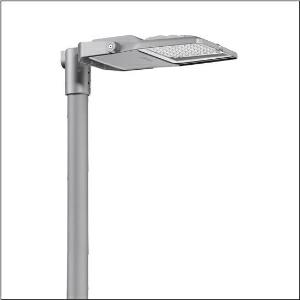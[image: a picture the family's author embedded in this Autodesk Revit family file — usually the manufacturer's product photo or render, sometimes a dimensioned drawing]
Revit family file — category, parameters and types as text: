
# Revit family: floodlight_fl_21_iq_mini___pl43_5xa7772c2a3a_c494
name_source: partatom
category: Lighting Fixtures
units: mm (PartAtom-declared; Revit-internal decimal feet)

## family parameters
Cut with Voids When Loaded = No
Host = Face
Light Source = No
Part Type = Normal
Room Calculation Point = No
Round Connector Dimension = Use Diameter
Shared = No

## types (1)
- --- (1 x LED, 12520 lm, 87.2 W, 3000K)
    Apparent Load = 87 VA
    CIE Flux Codes = 27 78 99 100 100
    Color Rendering = 70
    Color Temperature = 3000K
    Default Elevation = 1800 mm
    Description = Floodlight FL 21 iQ mini, floodlight, primary light control with lens, of PMMA, primary optical cover: protective disc, of toughened safety glass, transparent, light distribution: PL43, light emission: direct distribution, installation type: surface-mounted, LED, High Power LED, rated luminous flux: 12.520lm, luminous efficacy: 144lm/W, light colour: 730, colour temperature: 3000K, control: Auto-Match, Temp-Guard, Night-Set, Smart-Wire, Desk-Remote (wireless, voltage-free reading and setting of iQ features in the workshop via application-optimized NFC function/RFID function), optimised constant luminous flux control (CLO 2.0), Light-Fading, Lumen-Switch, with terminal, 6-pole, mains connection: 220..240V, AC, 50/60Hz, start of lifetime: 87W, end of service life: 92W, reduction: 40W, luminaire housing, of diecast aluminium, powder-coated, Siteco® metallic grey (DB 702S), corrosivity category C5 mid according to DIN EN ISO 12944, sealing non-destructively replaceable, please order mast flange separately, mast bracket, of steel, galvanised, powder-coated, protection rating (complete): IP66, insulation class (complete): insulation class II (safety insulation), certification: CE, ENEC, VDE, protection symbol: D, impact resistance: IK08, permissible operating ambient temperature: -40..+40°C, permissible operating ambient temperature for outdoor applications: -40..+50°C, standard: DIN EN 12944, LABS conformity tested according to VDMA 24364:2018-05, packaging unit: 1 piece

Light Distribution: PL43
    Height = 70 mm
    Lamp = 1 x LED
    Lamp Light Flux = 12520 lm
    Lamp Power = 87.2 W
    Lamp count = 1
    Length = 485 mm
    Luminous efficacy = 144 lm/W
    Manufacturer = Siteco
    ModVariant = No
    Model = 5XA7772C2A3A
    Number of Poles = 1
    OnlyDefault = Yes
    Power Factor = 1
    Product Name = Floodlight FL 21 iQ mini | PL43
    Product group = floodlight | pylon annexe
    ProductGroupID = 6200
    Protection Class = Protection class II
    Protection Degree = IP 66
    RLX_Detail_Level = 1
    RLX_Emergency_Light_Flux = 0 lm
    RLX_Emergency_Type = 0
    RLX_Emergency_Type_DB = No
    RlxData = <blob elided: 101193 chars, md5=053aa3c9>
    Socket = socket
    Standby Power = 0 W
    System Light Flux = 12520 lm
    System Power = 87 W
    Type Comments = factory setting: luminous flux: 100 % | dim-lin: 254 | 456 mA
    Type Image = l_1007125.jpg
    URL = http://relux.com
    VarID = @adj_094605
    Voltage = 0 V
    Weight = 0.00 kg
    Width = 337 mm

## geometry (parser evidence)
native form markers: Blend x4, Sweep x11
no freeform markers — native parametric forms only
